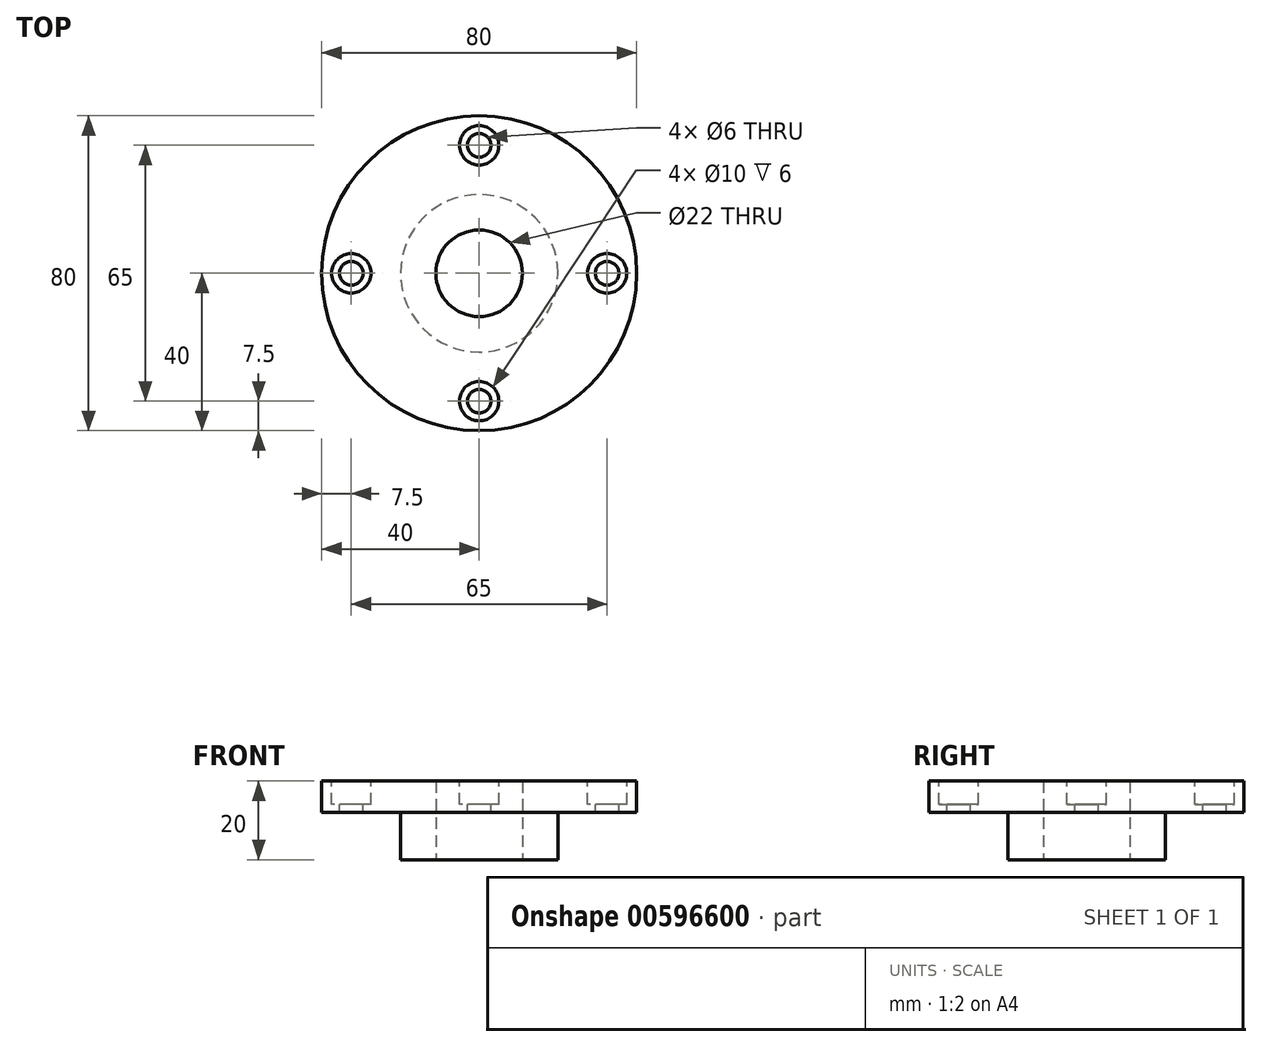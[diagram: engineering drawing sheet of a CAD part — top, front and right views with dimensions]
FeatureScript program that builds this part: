
annotation { "Feature Type Name" : "Feature", "Feature Type Description" : "" }
export const myFeature = defineFeature(function(context is Context, id is Id, definition is map)
    precondition{}
    {
        {
            var Q0;
            Q0=qCreatedBy(makeId("Front.planeOp"),FACE);
            var sketch = newSketch(context, id + "F0", { "sketchPlane" : qUnion([Q0])});
            skLineSegment(sketch, "E0", {"start": v(0, 0) * mm, "end": v(0, 20) * mm});
            skLineSegment(sketch, "E1.0", {"start": v(11, 0) * mm, "end": v(11, 20) * mm});
            skLineSegment(sketch, "E2.0", {"start": v(20, 0) * mm, "end": v(20, 12) * mm});
            skLineSegment(sketch, "E3", {"start": v(11, 20) * mm, "end": v(40, 20) * mm});
            skLineSegment(sketch, "E4.0", {"start": v(20, 12) * mm, "end": v(40, 12) * mm});
            skLineSegment(sketch, "E5", {"start": v(11, 0) * mm, "end": v(20, 0) * mm});
            skLineSegment(sketch, "E6", {"start": v(40, 12) * mm, "end": v(40, 20) * mm});
            skSolve(sketch);
        }
        {
            var Q0;
            Q0=makeQuery(id+"F0.imprint","IMPRINT",FACE,{"disambiguationData":[TD([[makeQuery(id+"F0.imprint","IMPRINT",EDGE,{"derivedFrom":sQuery(id+"F0.wireOp",EDGE,"E1.0")}),-1.0]])]});
            var Q1;
            Q1=sQuery(id+"F0.wireOp",EDGE,"E0");
            revolve(context, id + "F1", {"entities" : qUnion([Q0]), "axis" : qUnion([Q1]), "revolveType" : RevolveType.FULL});
        }
        {
            var Q0;
            Q0=makeQuery(id+"F1.opRevolve","SWEPT_FACE",FACE,{"disambiguationData":[OSD([sQuery(id+"F0.wireOp",EDGE,"E3")])]});
            var sketch = newSketch(context, id + "F2", { "sketchPlane" : qUnion([Q0])});
            skCircle(sketch, "E7", {"center": v(0, 32.5) * mm, "radius": 3 * mm});
            skCircle(sketch, "E8.1.0", {"center": v(-32.5, 0) * mm, "radius": 3 * mm});
            skCircle(sketch, "E8.2.0", {"center": v(0, -32.5) * mm, "radius": 3 * mm});
            skCircle(sketch, "E8.3.0", {"center": v(32.5, 0) * mm, "radius": 3 * mm});
            skPoint(sketch, "E8.center", {"position": v(0, 0) * mm});
            skSolve(sketch);
        }
        {
            var Q0;
            Q0 = qSketchRegion(id + "F2", true);
            extrude(context, id + "F3", {"entities" : qUnion([Q0]), "operationType" : NewBodyOperationType.REMOVE, "endBound" : BoundingType.THROUGH_ALL, "oppositeDirection" : true, "depth" : 25 * mm, "offsetDistance" : 25 * mm});
        }
        {
            var Q0;
            Q0=makeQuery(id+"F1.opRevolve","SWEPT_FACE",FACE,{"disambiguationData":[OSD([sQuery(id+"F0.wireOp",EDGE,"E3")])]});
            var sketch = newSketch(context, id + "F4", { "sketchPlane" : qUnion([Q0])});
            skCircle(sketch, "E9", {"center": v(0, 32.5) * mm, "radius": 5 * mm});
            skCircle(sketch, "E10.1.0", {"center": v(-32.5, 0) * mm, "radius": 5 * mm});
            skCircle(sketch, "E10.2.0", {"center": v(0, -32.5) * mm, "radius": 5 * mm});
            skCircle(sketch, "E10.3.0", {"center": v(32.5, 0) * mm, "radius": 5 * mm});
            skPoint(sketch, "E10.center", {"position": v(0, 0) * mm});
            skSolve(sketch);
        }
        {
            var Q0;
            Q0 = qSketchRegion(id + "F4", true);
            extrude(context, id + "F5", {"entities" : qUnion([Q0]), "operationType" : NewBodyOperationType.REMOVE, "oppositeDirection" : true, "depth" : 6 * mm, "offsetDistance" : 25 * mm});
        }
    });
